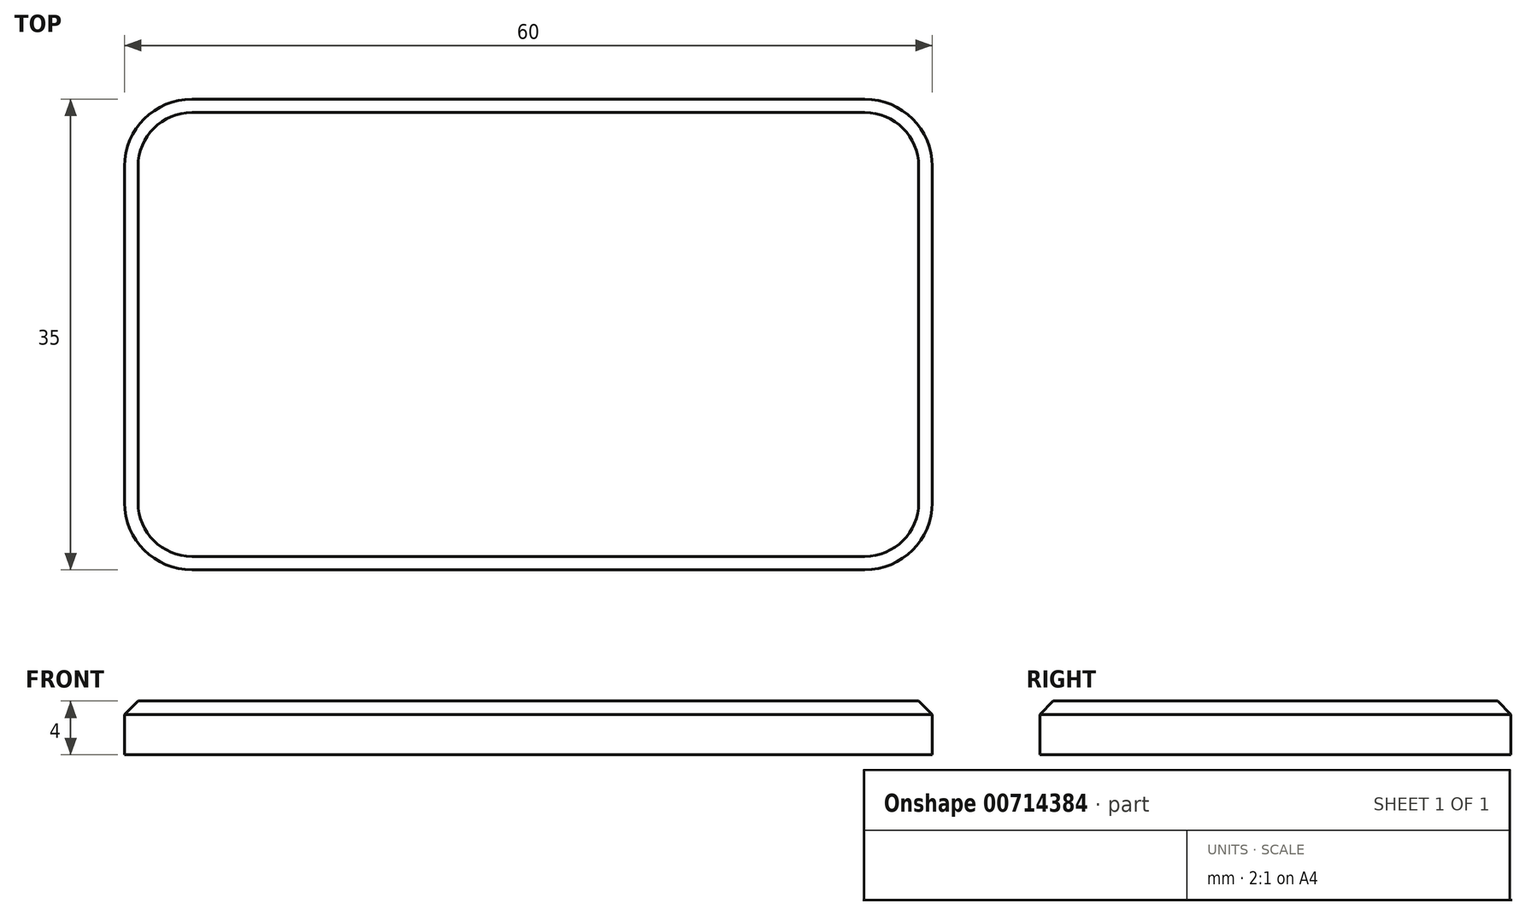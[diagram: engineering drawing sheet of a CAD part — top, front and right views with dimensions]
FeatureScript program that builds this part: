
annotation { "Feature Type Name" : "Feature", "Feature Type Description" : "" }
export const myFeature = defineFeature(function(context is Context, id is Id, definition is map)
    precondition{}
    {
        {
            var Q0;
            Q0=qCreatedBy(makeId("Top.planeOp"),FACE);
            var sketch = newSketch(context, id + "F0", { "sketchPlane" : qUnion([Q0])});
            skLineSegment(sketch, "E0.bottom", {"start": v(-30, 17.5) * mm, "end": v(30, 17.5) * mm});
            skLineSegment(sketch, "E0.top", {"start": v(-30, -17.5) * mm, "end": v(30, -17.5) * mm});
            skLineSegment(sketch, "E0.left", {"start": v(-30, 17.5) * mm, "end": v(-30, -17.5) * mm});
            skLineSegment(sketch, "E0.right", {"start": v(30, 17.5) * mm, "end": v(30, -17.5) * mm});
            skSolve(sketch);
        }
        {
            var Q0;
            Q0=makeQuery(id+"F0.imprint","IMPRINT",FACE,{"disambiguationData":[TD([[makeQuery(id+"F0.imprint","IMPRINT",EDGE,{"derivedFrom":sQuery(id+"F0.wireOp",EDGE,"E0.bottom")}),-1.0]])]});
            extrude(context, id + "F1", {"entities" : qUnion([Q0]), "depth" : 4 * mm, "offsetDistance" : 25 * mm});
        }
        {
            var Q0;
            Q0=makeQuery(id+"F1.opExtrude","SWEPT_EDGE",EDGE,{"disambiguationData":[OSD([sQuery(id+"F0.wireOp",EDGE,"E0.bottom"),sQuery(id+"F0.wireOp",EDGE,"E0.left")])]});
            var Q1;
            Q1=makeQuery(id+"F1.opExtrude","SWEPT_EDGE",EDGE,{"disambiguationData":[OSD([sQuery(id+"F0.wireOp",EDGE,"E0.top"),sQuery(id+"F0.wireOp",EDGE,"E0.left")])]});
            var Q2;
            Q2=makeQuery(id+"F1.opExtrude","SWEPT_EDGE",EDGE,{"disambiguationData":[OSD([sQuery(id+"F0.wireOp",EDGE,"E0.top"),sQuery(id+"F0.wireOp",EDGE,"E0.right")])]});
            var Q3;
            Q3=makeQuery(id+"F1.opExtrude","SWEPT_EDGE",EDGE,{"disambiguationData":[OSD([sQuery(id+"F0.wireOp",EDGE,"E0.bottom"),sQuery(id+"F0.wireOp",EDGE,"E0.right")])]});
            fillet(context, id + "F2", {"entities" : qUnion([Q0, Q1, Q2, Q3]), "radius" : 5 * mm, "tangentPropagation" : true, "allowEdgeOverflow" : false});
        }
        {
            var Q0;
            Q0=makeQuery(id+"F1.opExtrude","CAP_EDGE",EDGE,{"disambiguationData":[OSD([sQuery(id+"F0.wireOp",EDGE,"E0.bottom")])],"isStart":false});
            var Q1;
            Q1=makeQuery(id+"F1.opExtrude","CAP_EDGE",EDGE,{"disambiguationData":[OSD([sQuery(id+"F0.wireOp",EDGE,"E0.left")])],"isStart":false});
            var Q2;
            Q2=makeQuery(id+"F1.opExtrude","CAP_EDGE",EDGE,{"disambiguationData":[OSD([sQuery(id+"F0.wireOp",EDGE,"E0.top")])],"isStart":false});
            var Q3;
            Q3=makeQuery(id+"F1.opExtrude","CAP_EDGE",EDGE,{"disambiguationData":[OSD([sQuery(id+"F0.wireOp",EDGE,"E0.right")])],"isStart":false});
            chamfer(context, id + "F3", {"entities" : qUnion([Q0, Q1, Q2, Q3]), "width" : 1 * mm, "tangentPropagation" : true});
        }
    });
